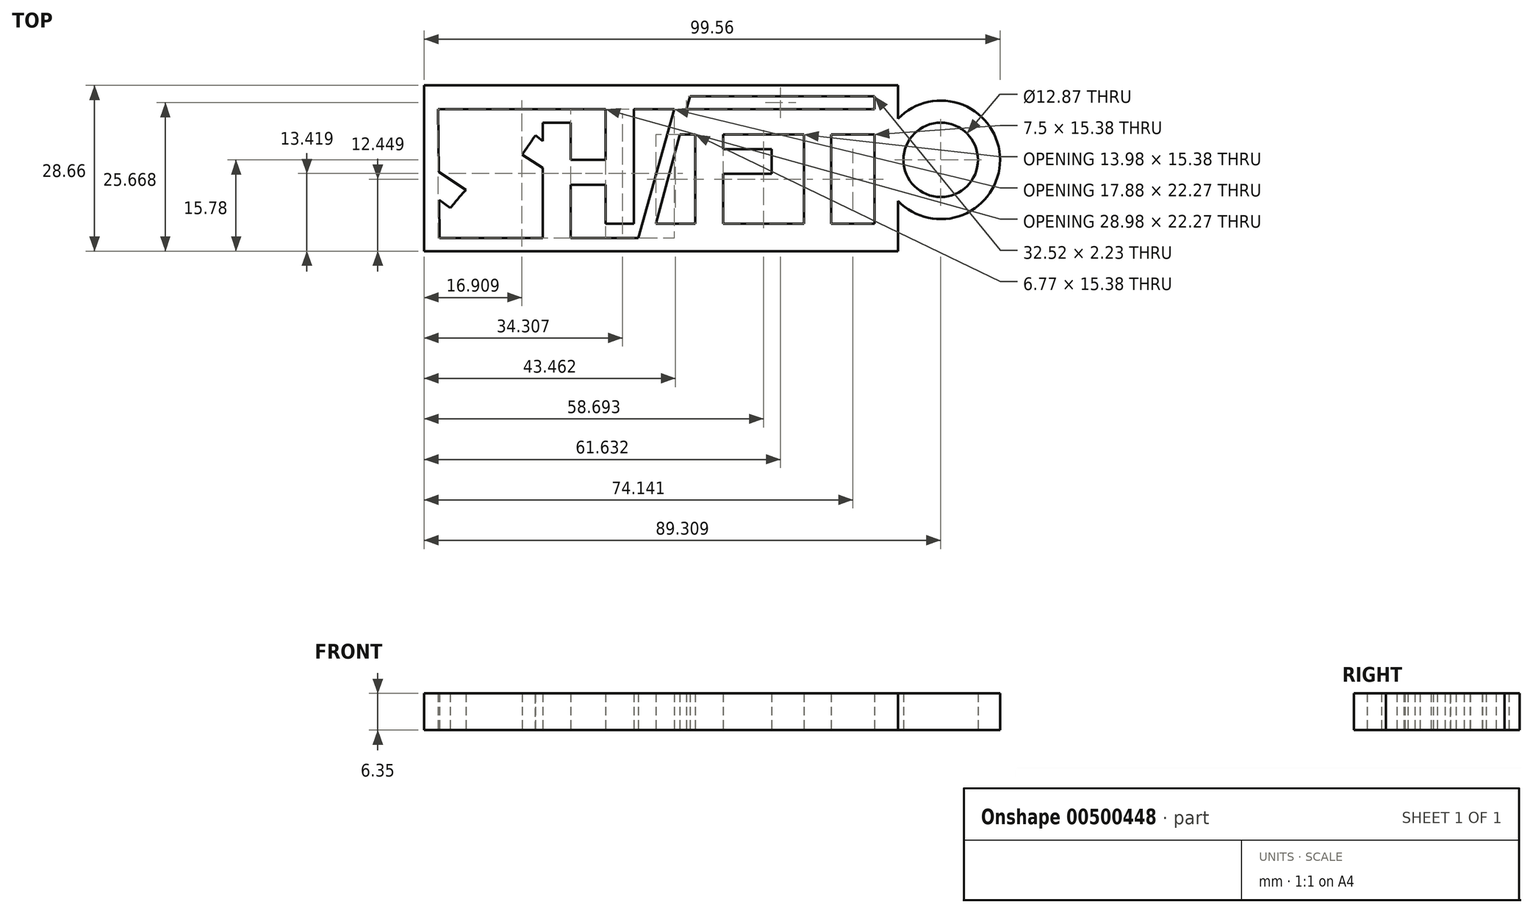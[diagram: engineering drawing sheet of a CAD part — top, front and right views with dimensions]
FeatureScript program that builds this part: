
annotation { "Feature Type Name" : "Feature", "Feature Type Description" : "" }
export const myFeature = defineFeature(function(context is Context, id is Id, definition is map)
    precondition{}
    {
        {
            var Q0;
            Q0=qCreatedBy(makeId("Top.planeOp"),FACE);
            var sketch = newSketch(context, id + "F0", { "sketchPlane" : qUnion([Q0])});
            skLineSegment(sketch, "E0.top", {"start": v(39.49, 12.88) * mm, "end": v(-39.49, 12.88) * mm});
            skLineSegment(sketch, "E0.right", {"start": v(-39.49, -12.88) * mm, "end": v(-39.49, 12.88) * mm});
            skPoint(sketch, "E0.middle", {"position": v(0, 0) * mm});
            skLineSegment(sketch, "E1", {"start": v(-37.07, 8.77) * mm, "end": v(-8.1, 8.77) * mm});
            skLineSegment(sketch, "E2", {"start": v(3.76, 8.77) * mm, "end": v(-2.43, -13.5) * mm});
            skLineSegment(sketch, "E3", {"start": v(-2.43, -13.5) * mm, "end": v(-14.12, -13.5) * mm});
            skLineSegment(sketch, "E4", {"start": v(-36.82, -13.5) * mm, "end": v(-36.9, -6.93) * mm});
            skLineSegment(sketch, "E5", {"start": v(6.48, 11) * mm, "end": v(38.4, 11) * mm});
            skLineSegment(sketch, "E6", {"start": v(38.4, 11) * mm, "end": v(38.4, 8.77) * mm});
            skLineSegment(sketch, "E7", {"start": v(38.4, -11.02) * mm, "end": v(30.9, -11.02) * mm});
            skLineSegment(sketch, "E8", {"start": v(0.59, -11.02) * mm, "end": v(4.7, 4.36) * mm});
            skLineSegment(sketch, "E9", {"start": v(7.36, 8.77) * mm, "end": v(36.2, 8.77) * mm});
            skLineSegment(sketch, "E10", {"start": v(36.2, 4.36) * mm, "end": v(30.9, 4.36) * mm});
            skLineSegment(sketch, "E11", {"start": v(30.9, 4.36) * mm, "end": v(30.9, -8.73) * mm});
            skLineSegment(sketch, "E12", {"start": v(26.2, -8.73) * mm, "end": v(26.2, 4.36) * mm});
            skLineSegment(sketch, "E13", {"start": v(26.2, 4.36) * mm, "end": v(12.21, 4.36) * mm});
            skLineSegment(sketch, "E14", {"start": v(12.21, 4.36) * mm, "end": v(12.21, 1.86) * mm});
            skLineSegment(sketch, "E15", {"start": v(12.21, 1.86) * mm, "end": v(20.6, 1.86) * mm});
            skLineSegment(sketch, "E16", {"start": v(20.6, 1.86) * mm, "end": v(20.6, -2.4) * mm});
            skLineSegment(sketch, "E17", {"start": v(20.6, -2.4) * mm, "end": v(12.21, -2.4) * mm});
            skLineSegment(sketch, "E18", {"start": v(12.21, -2.4) * mm, "end": v(12.21, -8.73) * mm});
            skLineSegment(sketch, "E19", {"start": v(7.36, -8.73) * mm, "end": v(7.36, 4.36) * mm});
            skLineSegment(sketch, "E20", {"start": v(-18.98, 6.42) * mm, "end": v(-14.12, 6.42) * mm});
            skLineSegment(sketch, "E21", {"start": v(-14.12, 6.42) * mm, "end": v(-14.12, 0) * mm});
            skLineSegment(sketch, "E22", {"start": v(-14.12, 0) * mm, "end": v(-8.1, 0) * mm});
            skLineSegment(sketch, "E23", {"start": v(-8.1, 0) * mm, "end": v(-8.1, 6.42) * mm});
            skLineSegment(sketch, "E24", {"start": v(-3.24, 6.42) * mm, "end": v(-3.24, -11.02) * mm});
            skLineSegment(sketch, "E25", {"start": v(-3.24, -11.02) * mm, "end": v(-8.1, -11.02) * mm});
            skLineSegment(sketch, "E26", {"start": v(-8.1, -11.02) * mm, "end": v(-8.1, -4.32) * mm});
            skLineSegment(sketch, "E27", {"start": v(-8.1, -4.32) * mm, "end": v(-14.12, -4.32) * mm});
            skLineSegment(sketch, "E28", {"start": v(-14.12, -4.32) * mm, "end": v(-14.12, -11.02) * mm});
            skLineSegment(sketch, "E29", {"start": v(-18.98, -11.02) * mm, "end": v(-18.98, -1.36) * mm});
            skFitSpline(sketch, "E30", {"points": [v(-20.3, 4.41) * mm, v(-22.58, 5.81) * mm, v(-26.6, 6.69) * mm, v(-30.45, 6.16) * mm, v(-33.6, 3.27) * mm, v(-34.04, 0) * mm, v(-32.9, -2.33) * mm, v(-29.05, -4.08) * mm, v(-25.9, -4.78) * mm, v(-24.59, -5.74) * mm, v(-24.68, -6.7) * mm, v(-26.6, -7.31) * mm, v(-29.93, -6.61) * mm, v(-32.03, -5.3) * mm, v(-32.18, -5.24) * mm, v(-32.24, -5.21) * mm, v(-34.9, -8.28) * mm, v(-34.96, -8.34) * mm, v(-34.93, -8.43) * mm, v(-33.56, -9.42) * mm, v(-30.76, -10.73) * mm, v(-26.83, -11.43) * mm, v(-22.98, -10.73) * mm, v(-20.09, -7.93) * mm, v(-19.74, -4.6) * mm, v(-21.05, -2.07) * mm, v(-26.74, 0) * mm, v(-28.31, 0.47) * mm, v(-29.1, 1.34) * mm, v(-28.84, 2.22) * mm, v(-27.35, 2.66) * mm, v(-24.9, 2.22) * mm, v(-23.06, 1.26) * mm, v(-22.71, 1) * mm, v(-22.54, 0.9) * mm, v(-22.45, 1) * mm, v(-20.29, 4.15) * mm, v(-20.22, 4.27) * mm, v(-20.3, 4.41) * mm]});
            skLineSegment(sketch, "E31", {"start": v(-39.49, -12.88) * mm, "end": v(-39.49, -15.78) * mm});
            skLineSegment(sketch, "E32", {"start": v(-39.49, -15.78) * mm, "end": v(42.44, -15.78) * mm});
            skLineSegment(sketch, "E33", {"start": v(39.49, 12.88) * mm, "end": v(42.44, 12.88) * mm});
            skLineSegment(sketch, "E34", {"start": v(42.44, -15.78) * mm, "end": v(42.44, -7.11) * mm});
            skLineSegment(sketch, "E35", {"start": v(36.2, 8.77) * mm, "end": v(38.4, 8.77) * mm});
            skLineSegment(sketch, "E36", {"start": v(36.2, 4.36) * mm, "end": v(38.4, 4.36) * mm});
            skLineSegment(sketch, "E37", {"start": v(26.2, -8.73) * mm, "end": v(26.2, -11.02) * mm});
            skLineSegment(sketch, "E38", {"start": v(30.9, -8.73) * mm, "end": v(30.9, -11.02) * mm});
            skLineSegment(sketch, "E39", {"start": v(7.36, 8.77) * mm, "end": v(5.88, 8.77) * mm});
            skLineSegment(sketch, "E40", {"start": v(7.36, -8.73) * mm, "end": v(7.36, -11.02) * mm});
            skLineSegment(sketch, "E41", {"start": v(12.21, -8.73) * mm, "end": v(12.21, -11.02) * mm});
            skLineSegment(sketch, "E42.trimOffspring", {"start": v(7.36, -11.02) * mm, "end": v(0.59, -11.02) * mm});
            skLineSegment(sketch, "E43.trimOffspring", {"start": v(38.4, 4.36) * mm, "end": v(38.4, -11.02) * mm});
            skLineSegment(sketch, "E44.trimOffspring", {"start": v(26.2, -11.02) * mm, "end": v(12.21, -11.02) * mm});
            skLineSegment(sketch, "E45", {"start": v(7.36, 4.36) * mm, "end": v(4.7, 4.36) * mm});
            skLineSegment(sketch, "E46.trimOffspring", {"start": v(5.88, 8.77) * mm, "end": v(6.48, 11) * mm});
            skLineSegment(sketch, "E47", {"start": v(-3.24, 6.42) * mm, "end": v(-3.24, 8.77) * mm});
            skLineSegment(sketch, "E48", {"start": v(-8.1, 6.42) * mm, "end": v(-8.1, 8.77) * mm});
            skLineSegment(sketch, "E49", {"start": v(-18.98, -11.02) * mm, "end": v(-18.98, -13.5) * mm});
            skPoint(sketch, "E49.endSnap0", {"position": v(-19.63, -13.5) * mm});
            skLineSegment(sketch, "E50", {"start": v(-14.12, -11.02) * mm, "end": v(-14.12, -13.5) * mm});
            skLineSegment(sketch, "E51.trimOffspring", {"start": v(-3.24, 8.77) * mm, "end": v(3.76, 8.77) * mm});
            skLineSegment(sketch, "E52.trimOffspring", {"start": v(-18.98, -13.5) * mm, "end": v(-36.82, -13.5) * mm});
            skLineSegment(sketch, "E53", {"start": v(-20.22, 4.27) * mm, "end": v(-18.98, 3.27) * mm});
            skLineSegment(sketch, "E54", {"start": v(-22.54, 0.9) * mm, "end": v(-18.98, -1.36) * mm});
            skLineSegment(sketch, "E55.trimOffspring", {"start": v(-18.98, 3.27) * mm, "end": v(-18.98, 6.42) * mm});
            skLineSegment(sketch, "E56", {"start": v(-32.18, -5.24) * mm, "end": v(-36.95, -2.08) * mm});
            skLineSegment(sketch, "E57", {"start": v(-34.96, -8.34) * mm, "end": v(-36.9, -6.93) * mm});
            skLineSegment(sketch, "E58.trimOffspring", {"start": v(-36.95, -2.08) * mm, "end": v(-37.07, 8.77) * mm});
            skArc(sketch, "E59", {"start": v(42.44, -7.11) * mm, "mid": v(60.07, 0) * mm, "end": v(42.44, 7.11) * mm});
            skCircle(sketch, "E60", {"center": v(49.82, 0) * mm, "radius": 6.43 * mm});
            skLineSegment(sketch, "E61.trimOffspring", {"start": v(42.44, 7.11) * mm, "end": v(42.44, 12.88) * mm});
            skSolve(sketch);
        }
        {
            var Q0;
            Q0 = qSketchRegion(id + "F0", true);
            extrude(context, id + "F1", {"entities" : qUnion([Q0]), "depth" : 6.35 * mm});
        }
    });
